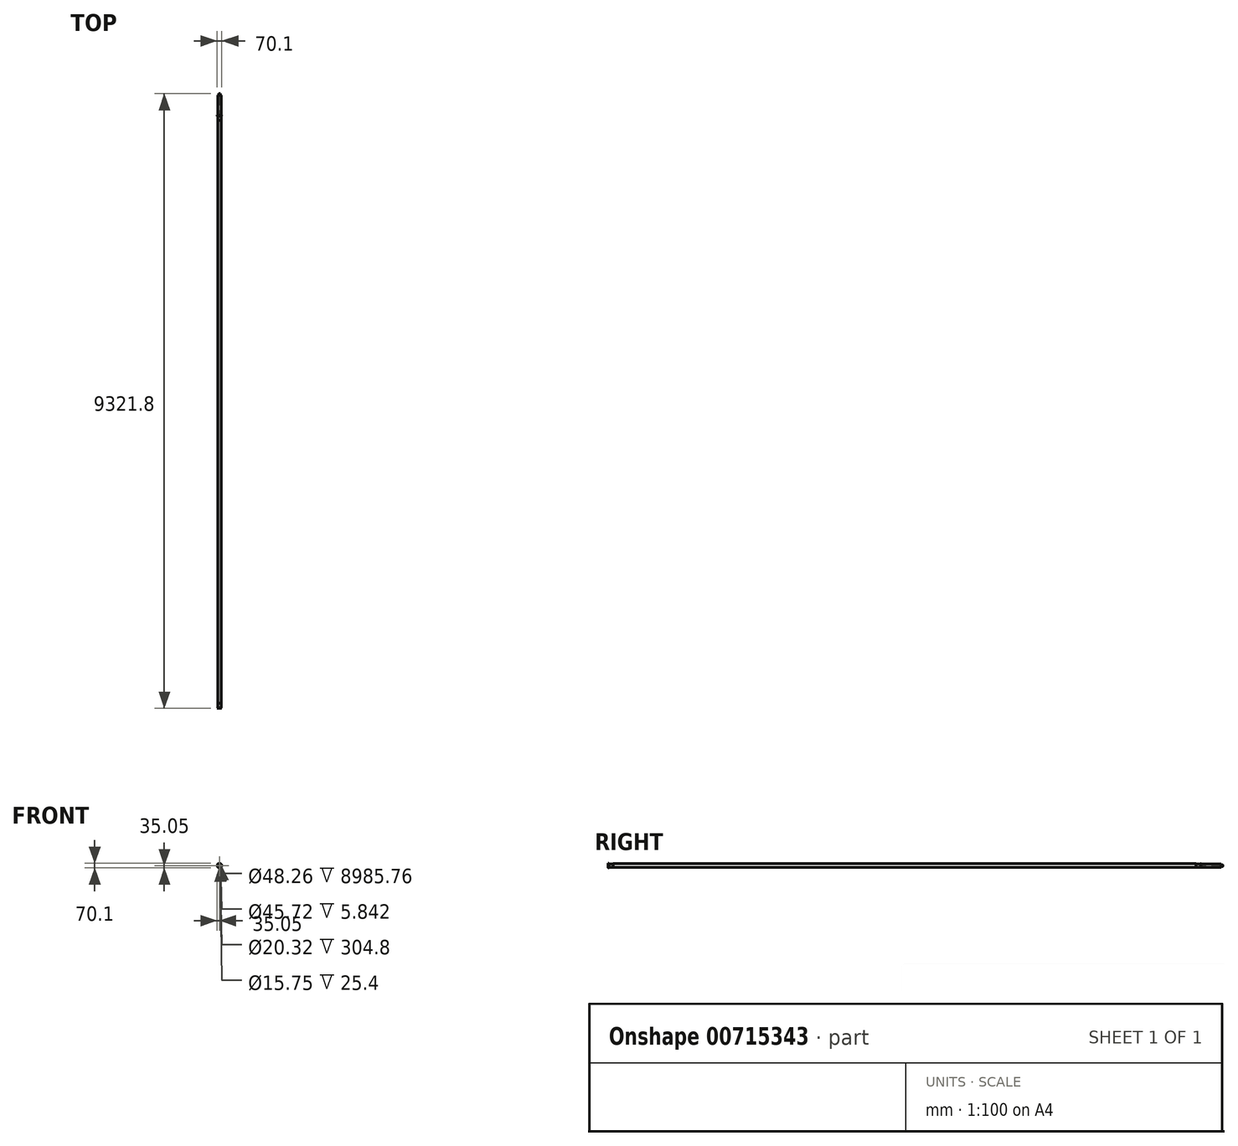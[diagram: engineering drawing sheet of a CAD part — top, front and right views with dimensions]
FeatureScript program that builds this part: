
annotation { "Feature Type Name" : "Feature", "Feature Type Description" : "" }
export const myFeature = defineFeature(function(context is Context, id is Id, definition is map)
    precondition{}
    {
        {
            var Q0;
            Q0=qCreatedBy(makeId("Front.planeOp"),FACE);
            var sketch = newSketch(context, id + "F0", { "sketchPlane" : qUnion([Q0])});
            skCircle(sketch, "E0", {"center": v(0, 0) * mm, "radius": 22.23 * mm, "construction": true});
            skSolve(sketch);
        }
        {
            var Q0;
            Q0=qCreatedBy(makeId("Front.planeOp"),FACE);
            var sketch = newSketch(context, id + "F1", { "sketchPlane" : qUnion([Q0])});
            skCircle(sketch, "E1", {"center": v(0, 0) * mm, "radius": 24.13 * mm});
            skCircle(sketch, "E2", {"center": v(0, 0) * mm, "radius": 35.05 * mm});
            skSolve(sketch);
        }
        {
            var Q0;
            Q0=qSketchRegion(id+"F1",true);
            extrude(context, id + "F2", {"entities" : qUnion([Q0]), "oppositeDirection" : true, "depth" : 5.84 * mm, "offsetDistance" : 25.4 * mm});
        }
        {
            var Q0;
            Q0=makeQuery(id+"F2.opExtrude","CAP_EDGE",EDGE,{"disambiguationData":[OSD([sQuery(id+"F1.wireOp",EDGE,"E2")])],"isStart":false});
            chamfer(context, id + "F3", {"entities" : qUnion([Q0]), "chamferType" : ChamferType.OFFSET_ANGLE, "width" : 2.54 * mm, "oppositeDirection" : false, "angle" : 70 * degree, "tangentPropagation" : true});
        }
        {
            var Q0;
            Q0=makeQuery(id+"F2.opExtrude","CAP_FACE",FACE,{"disambiguationData":[OSD([sQuery(id+"F1.wireOp",EDGE,"E1"),sQuery(id+"F1.wireOp",EDGE,"E2")])],"isStart":false});
            var sketch = newSketch(context, id + "F4", { "sketchPlane" : qUnion([Q0])});
            skCircle(sketch, "E3", {"center": v(0, 0) * mm, "radius": 28.07 * mm});
            skCircle(sketch, "E4", {"center": v(0, 0) * mm, "radius": 24.13 * mm});
            skSolve(sketch);
        }
        {
            var Q0;
            Q0=qSketchRegion(id+"F4",true);
            extrude(context, id + "F5", {"entities" : qUnion([Q0]), "operationType" : NewBodyOperationType.ADD, "depth" : 2.54 * mm, "offsetDistance" : 25.4 * mm});
        }
        {
            var Q0;
            Q0=makeQuery(id+"F5.opExtrude","CAP_FACE",FACE,{"disambiguationData":[OSD([sQuery(id+"F4.wireOp",EDGE,"E3"),sQuery(id+"F4.wireOp",EDGE,"E4")])],"isStart":false});
            var sketch = newSketch(context, id + "F6", { "sketchPlane" : qUnion([Q0])});
            skCircle(sketch, "E5", {"center": v(0, 0) * mm, "radius": 26.55 * mm});
            skCircle(sketch, "E6", {"center": v(0, 0) * mm, "radius": 24.13 * mm});
            skSolve(sketch);
        }
        {
            var Q0;
            Q0=qSketchRegion(id+"F6",true);
            extrude(context, id + "F7", {"entities" : qUnion([Q0]), "operationType" : NewBodyOperationType.ADD, "depth" : 2.54 * mm, "offsetDistance" : 25.4 * mm});
        }
        {
            var Q0;
            Q0=makeQuery(id+"F7.opExtrude","CAP_FACE",FACE,{"disambiguationData":[OSD([sQuery(id+"F6.wireOp",EDGE,"E5"),sQuery(id+"F6.wireOp",EDGE,"E6")])],"isStart":false});
            var sketch = newSketch(context, id + "F8", { "sketchPlane" : qUnion([Q0])});
            skCircle(sketch, "E7", {"center": v(0, 0) * mm, "radius": 24.13 * mm});
            skCircle(sketch, "E8", {"center": v(0, 0) * mm, "radius": 25.4 * mm});
            skSolve(sketch);
        }
        {
            var Q0;
            Q0=qSketchRegion(id+"F8",true);
            extrude(context, id + "F9", {"entities" : qUnion([Q0]), "operationType" : NewBodyOperationType.ADD, "depth" : 65.28 * mm, "offsetDistance" : 25.4 * mm});
        }
        {
            var Q0;
            Q0=makeQuery(id+"F9.opExtrude","CAP_FACE",FACE,{"disambiguationData":[OSD([sQuery(id+"F8.wireOp",EDGE,"E7"),sQuery(id+"F8.wireOp",EDGE,"E8")])],"isStart":false});
            var sketch = newSketch(context, id + "F10", { "sketchPlane" : qUnion([Q0])});
            skCircle(sketch, "E9", {"center": v(0, 0) * mm, "radius": 27.94 * mm});
            skCircle(sketch, "E10", {"center": v(0, 0) * mm, "radius": 24.13 * mm});
            skSolve(sketch);
        }
        {
            var Q0;
            Q0=qCreatedBy(makeId("Right.planeOp"),FACE);
            var sketch = newSketch(context, id + "F11", { "sketchPlane" : qUnion([Q0])});
            skLineSegment(sketch, "E11", {"start": v(76.2, 0) * mm, "end": v(8915.4, 0) * mm});
            skSolve(sketch);
        }
        {
            var Q0;
            Q0=qSketchRegion(id+"F10",true);
            var Q1;
            Q1=qConstructionFilter(qBodyType(qCreatedBy(id+"F11",EDGE),BodyType.WIRE),ConstructionObject.NO);
            sweep(context, id + "F12", {"operationType" : NewBodyOperationType.ADD, "profiles" : qUnion([Q0]), "path" : qUnion([Q1])});
        }
        {
            var Q0;
            Q0=makeQuery(id+"F12.opSweep","CAP_FACE",FACE,{"disambiguationData":[OSD([sQuery(id+"F10.wireOp",EDGE,"E9"),sQuery(id+"F10.wireOp",EDGE,"E10"),sQuery(id+"F11.wireOp",VERTEX,"7ykRA0Qg-2DrY-rTCa-7tXY-ZQoEE0Xzwcjr.end")])],"isStart":false});
            var sketch = newSketch(context, id + "F13", { "sketchPlane" : qUnion([Q0])});
            skCircle(sketch, "E12", {"center": v(0, 0) * mm, "radius": 24.13 * mm});
            skCircle(sketch, "E13", {"center": v(0, 0) * mm, "radius": 25.4 * mm});
            skSolve(sketch);
        }
        {
            var Q0;
            Q0=makeQuery(id+"F12.opSweep","CAP_EDGE",EDGE,{"disambiguationData":[OSD([sQuery(id+"F10.wireOp",EDGE,"E9"),sQuery(id+"F11.wireOp",VERTEX,"7ykRA0Qg-2DrY-rTCa-7tXY-ZQoEE0Xzwcjr.end")])],"isStart":false});
            fillet(context, id + "F14", {"entities" : qUnion([Q0]), "radius" : 1.27 * mm, "tangentPropagation" : true, "allowEdgeOverflow" : false});
        }
        {
            var Q0;
            Q0=qSketchRegion(id+"F13",true);
            extrude(context, id + "F15", {"entities" : qUnion([Q0]), "operationType" : NewBodyOperationType.ADD, "depth" : 76.2 * mm, "offsetDistance" : 25.4 * mm});
        }
        {
            var Q0;
            Q0=makeQuery(id+"F15.opExtrude","CAP_FACE",FACE,{"disambiguationData":[OSD([sQuery(id+"F13.wireOp",EDGE,"E12"),sQuery(id+"F13.wireOp",EDGE,"E13")])],"isStart":false});
            var sketch = newSketch(context, id + "F16", { "sketchPlane" : qUnion([Q0])});
            skCircle(sketch, "E14", {"center": v(0, 0) * mm, "radius": 35.05 * mm});
            skCircle(sketch, "E15", {"center": v(0, 0) * mm, "radius": 22.86 * mm});
            skSolve(sketch);
        }
        {
            var Q0;
            Q0=qSketchRegion(id+"F16",true);
            extrude(context, id + "F17", {"entities" : qUnion([Q0]), "operationType" : NewBodyOperationType.ADD, "oppositeDirection" : true, "depth" : 5.84 * mm, "offsetDistance" : 25.4 * mm});
        }
        {
            var Q0;
            Q0=makeQuery(id+"F17.opExtrude","CAP_EDGE",EDGE,{"disambiguationData":[OSD([sQuery(id+"F16.wireOp",EDGE,"E14")])],"isStart":false});
            chamfer(context, id + "F18", {"entities" : qUnion([Q0]), "chamferType" : ChamferType.OFFSET_ANGLE, "width" : 2.54 * mm, "oppositeDirection" : false, "angle" : 70 * degree, "tangentPropagation" : true});
        }
        {
            var Q0;
            Q0=makeQuery(id+"F17.opExtrude","CAP_FACE",FACE,{"disambiguationData":[OSD([sQuery(id+"F16.wireOp",EDGE,"E14"),sQuery(id+"F16.wireOp",EDGE,"E15")])],"isStart":false});
            var sketch = newSketch(context, id + "F19", { "sketchPlane" : qUnion([Q0])});
            skCircle(sketch, "E16", {"center": v(0, 0) * mm, "radius": 24.13 * mm});
            skCircle(sketch, "E17", {"center": v(0, 0) * mm, "radius": 28.07 * mm});
            skSolve(sketch);
        }
        {
            var Q0;
            Q0=qSketchRegion(id+"F19",true);
            extrude(context, id + "F20", {"entities" : qUnion([Q0]), "operationType" : NewBodyOperationType.ADD, "depth" : 2.54 * mm, "offsetDistance" : 25.4 * mm});
        }
        {
            var Q0;
            Q0=makeQuery(id+"F20.opExtrude","CAP_FACE",FACE,{"disambiguationData":[OSD([sQuery(id+"F19.wireOp",EDGE,"E16"),sQuery(id+"F19.wireOp",EDGE,"E17")])],"isStart":false});
            var sketch = newSketch(context, id + "F21", { "sketchPlane" : qUnion([Q0])});
            skCircle(sketch, "E18", {"center": v(0, 0) * mm, "radius": 24.13 * mm});
            skCircle(sketch, "E19", {"center": v(0, 0) * mm, "radius": 26.8 * mm});
            skSolve(sketch);
        }
        {
            var Q0;
            Q0=qSketchRegion(id+"F21",true);
            extrude(context, id + "F22", {"entities" : qUnion([Q0]), "operationType" : NewBodyOperationType.ADD, "depth" : 2.54 * mm, "offsetDistance" : 25.4 * mm});
        }
        {
            var Q0;
            Q0=makeQuery(id+"F17.boolean.opBoolean","MERGE",FACE,{"derivedFrom":[makeQuery(id+"F15.opExtrude","CAP_FACE",FACE,{"disambiguationData":[OSD([sQuery(id+"F13.wireOp",EDGE,"E12"),sQuery(id+"F13.wireOp",EDGE,"E13")])],"isStart":false}),makeQuery(id+"F17.opExtrude","CAP_FACE",FACE,{"disambiguationData":[OSD([sQuery(id+"F16.wireOp",EDGE,"E14"),sQuery(id+"F16.wireOp",EDGE,"E15")])],"isStart":true})]});
            var sketch = newSketch(context, id + "F23", { "sketchPlane" : qUnion([Q0])});
            skCircle(sketch, "E20", {"center": v(0, 0) * mm, "radius": 10.16 * mm});
            skCircle(sketch, "E21", {"center": v(0, 0) * mm, "radius": 24.13 * mm});
            skSolve(sketch);
        }
        {
            var Q0;
            Q0=qSketchRegion(id+"F23",true);
            extrude(context, id + "F24", {"entities" : qUnion([Q0]), "operationType" : NewBodyOperationType.ADD, "depth" : 304.8 * mm, "offsetDistance" : 25.4 * mm});
        }
        {
            var Q0;
            Q0=makeQuery(id+"F24.opExtrude","CAP_FACE",FACE,{"disambiguationData":[OSD([sQuery(id+"F23.wireOp",EDGE,"E20"),sQuery(id+"F23.wireOp",EDGE,"E21")])],"isStart":false});
            var sketch = newSketch(context, id + "F25", { "sketchPlane" : qUnion([Q0])});
            skCircle(sketch, "E22", {"center": v(0, 0) * mm, "radius": 10.67 * mm});
            skCircle(sketch, "E23", {"center": v(0, 0) * mm, "radius": 7.87 * mm});
            skSolve(sketch);
        }
        {
            var Q0;
            Q0 = qSketchRegion(id + "F25", true);
            extrude(context, id + "F26", {"entities" : qUnion([Q0]), "operationType" : NewBodyOperationType.ADD, "depth" : 25.4 * mm, "offsetDistance" : 25.4 * mm});
        }
    });
